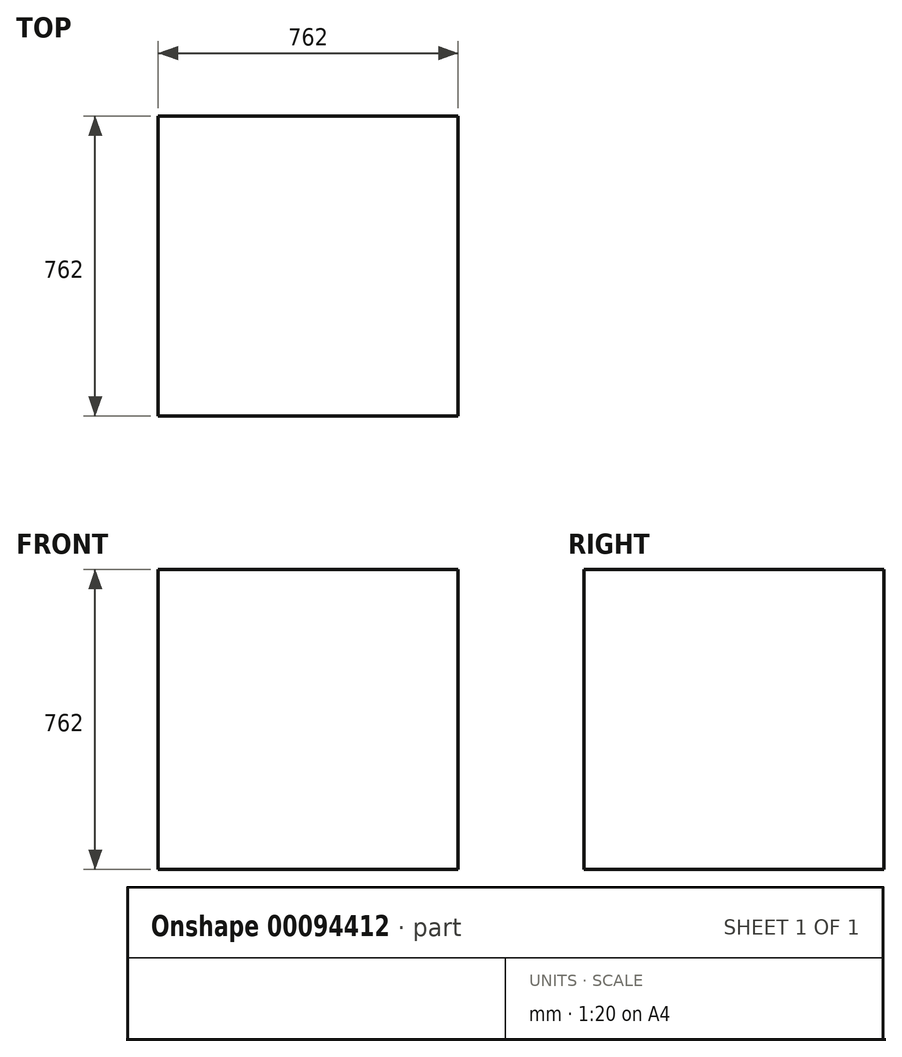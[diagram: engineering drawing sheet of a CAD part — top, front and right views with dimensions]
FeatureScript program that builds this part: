
annotation { "Feature Type Name" : "Feature", "Feature Type Description" : "" }
export const myFeature = defineFeature(function(context is Context, id is Id, definition is map)
    precondition{}
    {
        {
            var Q0;
            Q0=qCreatedBy(makeId("Top.planeOp"),FACE);
            var sketch = newSketch(context, id + "F0", { "sketchPlane" : qUnion([Q0])});
            skLineSegment(sketch, "E0.bottom", {"start": v(-381, 381) * mm, "end": v(381, 381) * mm});
            skLineSegment(sketch, "E0.top", {"start": v(-381, -381) * mm, "end": v(381, -381) * mm});
            skLineSegment(sketch, "E0.left", {"start": v(-381, 381) * mm, "end": v(-381, -381) * mm});
            skLineSegment(sketch, "E0.right", {"start": v(381, 381) * mm, "end": v(381, -381) * mm});
            skPoint(sketch, "E0.middle", {"position": v(0, 0) * mm});
            skSolve(sketch);
        }
        {
            var Q0;
            Q0 = qSketchRegion(id + "F0", true);
            extrude(context, id + "F1", {"entities" : qUnion([Q0]), "depth" : 762 * mm});
        }
    });
